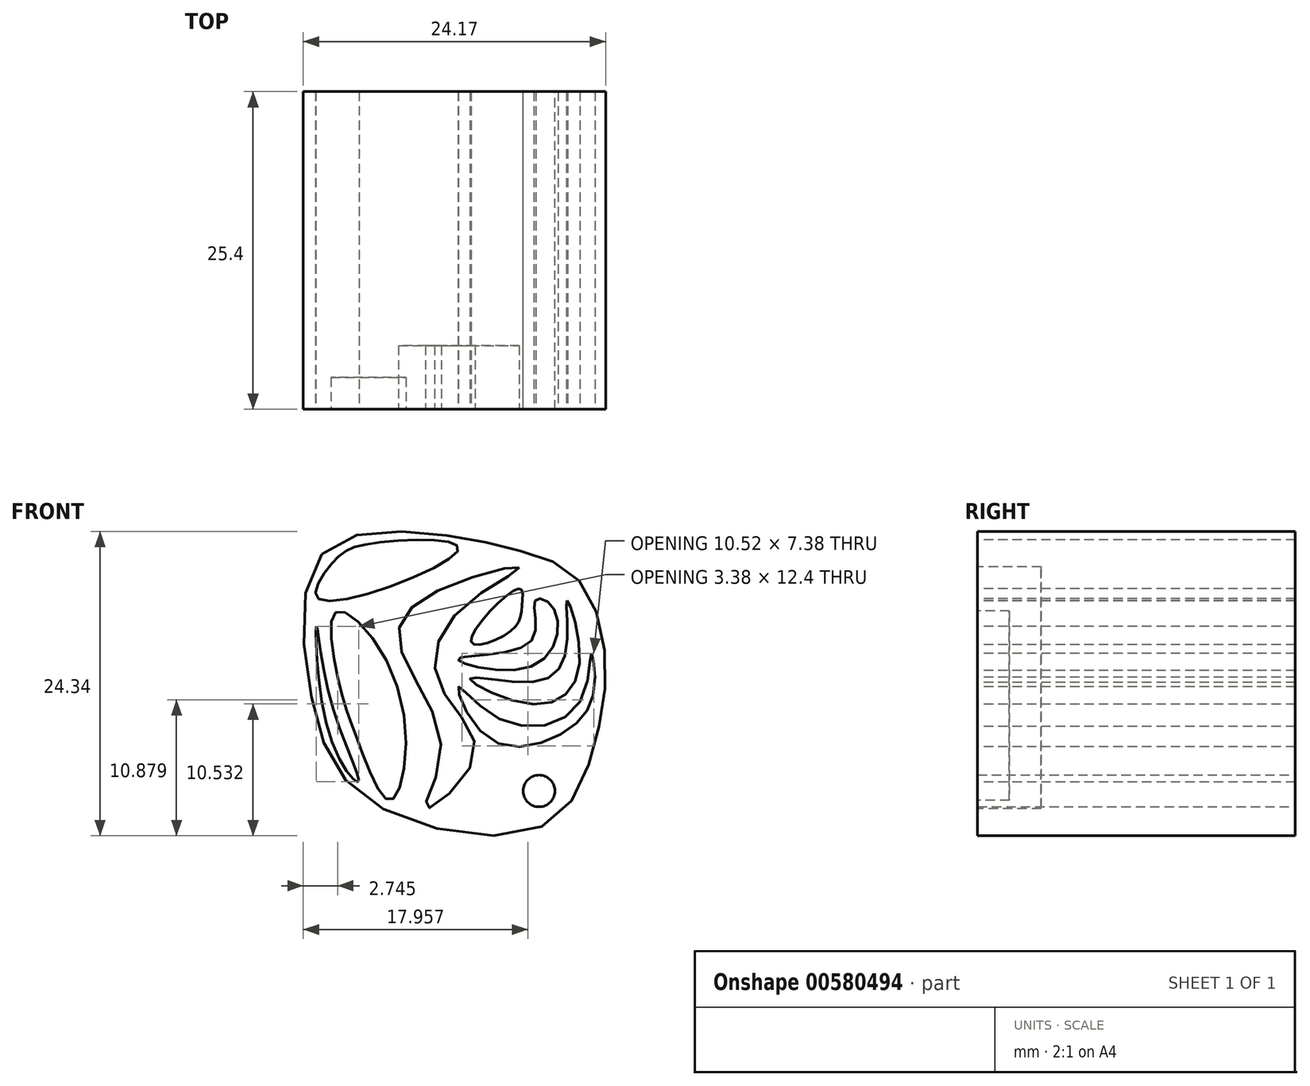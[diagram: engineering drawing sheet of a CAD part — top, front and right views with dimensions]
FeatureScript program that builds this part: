
annotation { "Feature Type Name" : "Feature", "Feature Type Description" : "" }
export const myFeature = defineFeature(function(context is Context, id is Id, definition is map)
    precondition{}
    {
        {
            var Q0;
            Q0=qCreatedBy(makeId("Front.planeOp"),FACE);
            var sketch = newSketch(context, id + "F0", { "sketchPlane" : qUnion([Q0])});
            skLineSegment(sketch, "E0.bottom", {"start": v(-22.02, 20.82) * mm, "end": v(3.38, 20.82) * mm});
            skLineSegment(sketch, "E0.top", {"start": v(-22.02, -4.58) * mm, "end": v(3.38, -4.58) * mm});
            skLineSegment(sketch, "E0.left", {"start": v(-22.02, 20.82) * mm, "end": v(-22.02, -4.58) * mm});
            skLineSegment(sketch, "E0.right", {"start": v(3.38, 20.82) * mm, "end": v(3.38, -4.58) * mm});
            skSolve(sketch);
        }
        {
            var Q0;
            Q0=makeQuery(id+"F0.imprint","IMPRINT",FACE,{"disambiguationData":[TD([[makeQuery(id+"F0.imprint","IMPRINT",EDGE,{"derivedFrom":sQuery(id+"F0.wireOp",EDGE,"E0.bottom")}),-1.0]])]});
            var sketch = newSketch(context, id + "F1", { "sketchPlane" : qUnion([Q0])});
            skFitSpline(sketch, "E1", {"points": [v(-19.6, 18.2) * mm, v(-11.03, 19.85) * mm, v(-3.76, 18.47) * mm, v(1, 16.05) * mm, v(3.07, 9.56) * mm, v(2.04, 2.38) * mm, v(-2.2, -3.68) * mm, v(-15.79, -1.52) * mm, v(-20.46, 6.96) * mm, v(-19.6, 18.2) * mm]});
            skSolve(sketch);
        }
        {
            var Q0;
            Q0 = qSketchRegion(id + "F1", true);
            extrude(context, id + "F2", {"entities" : qUnion([Q0]), "depth" : 25.4 * mm, "offsetDistance" : 25.4 * mm});
        }
        {
            var Q0;
            Q0=makeQuery(id+"F2.opExtrude","CAP_FACE",FACE,{"disambiguationData":[OSD([sQuery(id+"F1.wireOp",EDGE,"E1")])],"isStart":false});
            var sketch = newSketch(context, id + "F3", { "sketchPlane" : qUnion([Q0])});
            skFitSpline(sketch, "E2", {"points": [v(-18.81, 17.43) * mm, v(-15.44, 19.07) * mm, v(-8.7, 18.55) * mm, v(-19.77, 14.57) * mm, v(-18.81, 17.43) * mm]});
            skFitSpline(sketch, "E3", {"points": [v(-20.03, 12.41) * mm, v(-18.81, 3.24) * mm, v(-16.65, 0) * mm, v(-18.81, 6.27) * mm, v(-20.03, 12.41) * mm]});
            skFitSpline(sketch, "E4", {"points": [v(-3.85, 15.44) * mm, v(-7.65, 11.2) * mm, v(-4.45, 12.07) * mm, v(-3.59, 14.14) * mm, v(-3.85, 15.44) * mm]});
            skFitSpline(sketch, "E5", {"points": [v(-2.55, 14.49) * mm, v(-2.9, 11.2) * mm, v(-8.7, 9.82) * mm, v(-2.64, 9.3) * mm, v(-1.08, 13.88) * mm, v(-2.55, 14.49) * mm]});
            skFitSpline(sketch, "E6", {"points": [v(0, 14.49) * mm, v(0, 10.85) * mm, v(-2.55, 8) * mm, v(-7.74, 8.26) * mm, v(-2.55, 6.18) * mm, v(1, 9.38) * mm, v(0, 14.49) * mm]});
            skFitSpline(sketch, "E7", {"points": [v(1.95, 10.25) * mm, v(0.91, 6.18) * mm, v(-5.5, 5.06) * mm, v(-8.7, 7.57) * mm, v(-6.18, 3.41) * mm, v(0, 4.1) * mm, v(2.2, 7.57) * mm, v(1.95, 10.25) * mm]});
            skSolve(sketch);
        }
        {
            var Q0;
            Q0 = qSketchRegion(id + "F3", true);
            extrude(context, id + "F4", {"entities" : qUnion([Q0]), "operationType" : NewBodyOperationType.REMOVE, "oppositeDirection" : true, "depth" : 25.4 * mm, "offsetDistance" : 25.4 * mm});
        }
        {
            var Q0;
            Q0=makeQuery(id+"F0.imprint","IMPRINT",FACE,{"disambiguationData":[TD([[makeQuery(id+"F0.imprint","IMPRINT",EDGE,{"derivedFrom":sQuery(id+"F0.wireOp",EDGE,"E0.bottom")}),-1.0]])]});
            var sketch = newSketch(context, id + "F5", { "sketchPlane" : qUnion([Q0])});
            skCircle(sketch, "E8", {"center": v(-2.23, -0.74) * mm, "radius": 1.58 * mm});
            skCircle(sketch, "E9", {"center": v(-5.9, -1.02) * mm, "radius": 1.45 * mm});
            skCircle(sketch, "E10", {"center": v(0, 1.92) * mm, "radius": 1.25 * mm});
            skCircle(sketch, "E11", {"center": v(-9.84, -1.75) * mm, "radius": 1.51 * mm});
            skCircle(sketch, "E12", {"center": v(-13.87, 0) * mm, "radius": 1.51 * mm});
            skSolve(sketch);
        }
        {
            var Q0;
            Q0=sQuery(id+"F5.wireOp",VERTEX,"E8.center");
            var Q1;
            Q1=makeQuery(id+"F2.opExtrude","SWEPT_BODY",BODY,{"disambiguationData":[OSD([sQuery(id+"F1.wireOp",EDGE,"E1")])]});
            hole(context, id + "F6", {"style" : HoleStyle.SIMPLE, "endStyle" : HoleEndStyle.THROUGH, "oppositeDirection" : true, "holeDiameter" : 2.54 * mm, "majorDiameter" : 6.35 * mm, "isTappedThrough" : true, "tappedDepth" : 12.7 * mm, "tapClearance" : 3, "locations" : qUnion([Q0]), "scope" : qUnion([Q1])});
        }
        {
            var Q0;
            Q0=makeQuery(id+"F2.opExtrude","CAP_FACE",FACE,{"disambiguationData":[OSD([sQuery(id+"F1.wireOp",EDGE,"E1")])],"isStart":false});
            var sketch = newSketch(context, id + "F7", { "sketchPlane" : qUnion([Q0])});
            skFitSpline(sketch, "E13", {"points": [v(-18.49, 13.56) * mm, v(-18.12, 7.5) * mm, v(-16.75, 3.38) * mm, v(-14.18, -1.48) * mm, v(-13.45, 7.23) * mm, v(-18.49, 13.56) * mm]});
            skSolve(sketch);
        }
        {
            var Q0;
            Q0 = qSketchRegion(id + "F7", true);
            extrude(context, id + "F8", {"entities" : qUnion([Q0]), "operationType" : NewBodyOperationType.REMOVE, "oppositeDirection" : true, "depth" : 2.54 * mm, "offsetDistance" : 25.4 * mm});
        }
        {
            var Q0;
            Q0=makeQuery(id+"F2.opExtrude","CAP_FACE",FACE,{"disambiguationData":[OSD([sQuery(id+"F1.wireOp",EDGE,"E1")])],"isStart":false});
            var sketch = newSketch(context, id + "F9", { "sketchPlane" : qUnion([Q0])});
            skFitSpline(sketch, "E14", {"points": [v(-3.81, 17.1) * mm, v(-8.67, 13.62) * mm, v(-10.14, 7.67) * mm, v(-7.39, 2.07) * mm, v(-11.24, -2.14) * mm, v(-10.05, 2.72) * mm, v(-13.44, 11.15) * mm, v(-10.32, 15.27) * mm, v(-3.81, 17.1) * mm]});
            skSolve(sketch);
        }
        {
            var Q0;
            Q0 = qSketchRegion(id + "F9", true);
            extrude(context, id + "F10", {"entities" : qUnion([Q0]), "operationType" : NewBodyOperationType.REMOVE, "oppositeDirection" : true, "depth" : 5.08 * mm, "offsetDistance" : 25.4 * mm});
        }
        {
            var Q0;
            Q0=makeQuery(id+"F0.imprint","IMPRINT",FACE,{"disambiguationData":[TD([[makeQuery(id+"F0.imprint","IMPRINT",EDGE,{"derivedFrom":sQuery(id+"F0.wireOp",EDGE,"E0.bottom")}),-1.0]])]});
            var sketch = newSketch(context, id + "F11", { "sketchPlane" : qUnion([Q0])});
            skFitSpline(sketch, "E15", {"points": [v(-7.55, 16) * mm, v(-13.24, 15) * mm, v(-17.64, 13.44) * mm, v(-18.28, 8.4) * mm, v(-15.07, 1.43) * mm, v(-9.3, -2.33) * mm, v(-4.62, 0) * mm, v(-8.74, 4.1) * mm, v(-9.84, 10.14) * mm, v(-6.82, 14.36) * mm, v(-3.98, 16.74) * mm, v(-7.55, 16) * mm]});
            skSolve(sketch);
        }
        {
            var Q0;
            Q0 = qSketchRegion(id + "F11", true);
            extrude(context, id + "F12", {"entities" : qUnion([Q0]), "operationType" : NewBodyOperationType.ADD, "depth" : 2.54 * mm, "offsetDistance" : 25.4 * mm});
        }
    });
